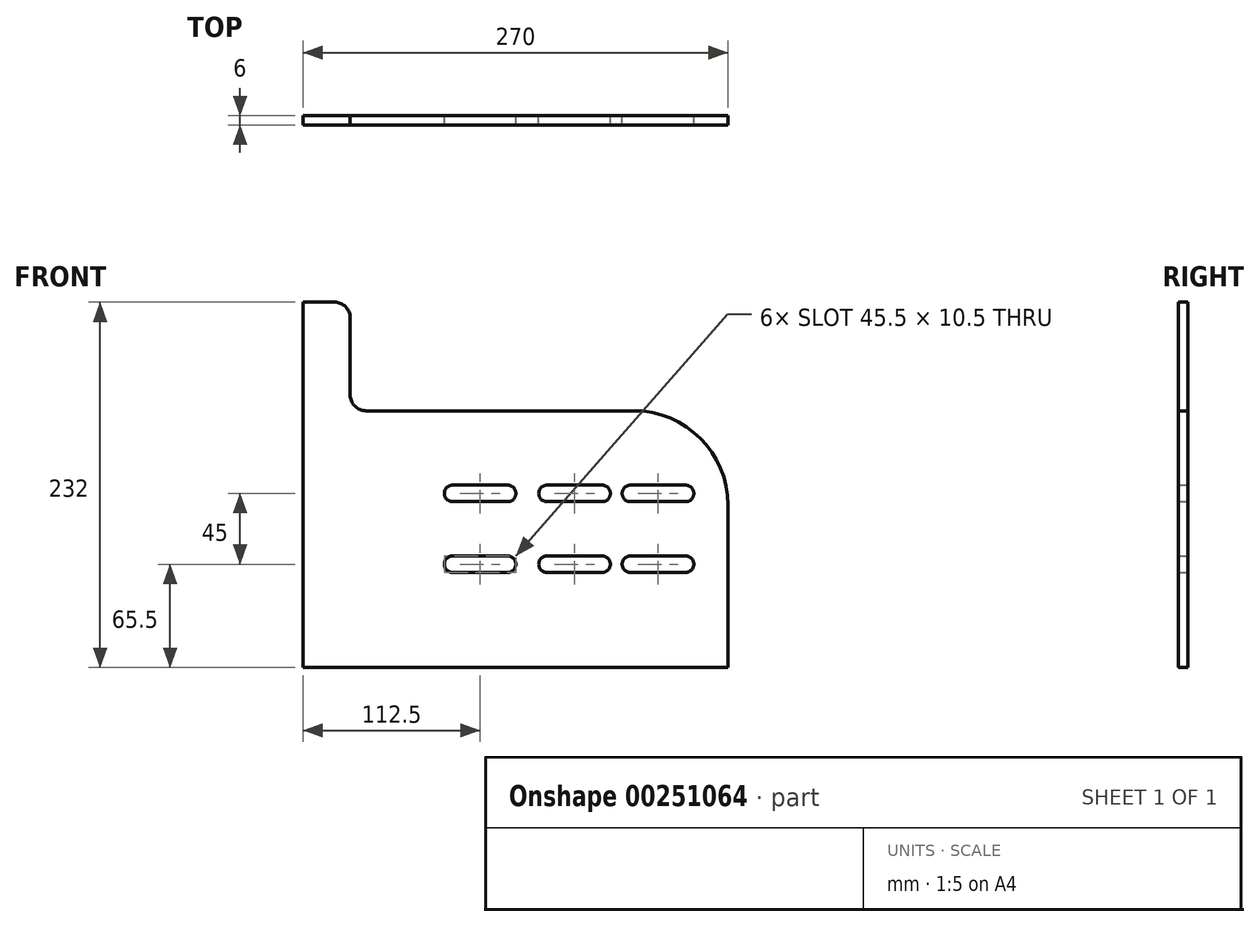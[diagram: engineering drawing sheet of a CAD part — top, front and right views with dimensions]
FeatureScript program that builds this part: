
annotation { "Feature Type Name" : "Feature", "Feature Type Description" : "" }
export const myFeature = defineFeature(function(context is Context, id is Id, definition is map)
    precondition{}
    {
        {
            var Q0;
            Q0=qCreatedBy(makeId("Front.planeOp"),FACE);
            var sketch = newSketch(context, id + "F0", { "sketchPlane" : qUnion([Q0])});
            skLineSegment(sketch, "E0.bottom", {"start": v(0, 0) * mm, "end": v(270, 0) * mm});
            skLineSegment(sketch, "E0.top", {"start": v(40, 163) * mm, "end": v(210, 163) * mm});
            skLineSegment(sketch, "E0.left", {"start": v(0, 0) * mm, "end": v(0, 163) * mm});
            skLineSegment(sketch, "E0.right", {"start": v(270, 0) * mm, "end": v(270, 103) * mm});
            skLineSegment(sketch, "E1.bottom", {"start": v(95, 115.75) * mm, "end": v(130, 115.75) * mm});
            skLineSegment(sketch, "E1.top", {"start": v(95, 105.25) * mm, "end": v(130, 105.25) * mm});
            skArc(sketch, "E2", {"start": v(95, 115.75) * mm, "mid": v(89.75, 110.5) * mm, "end": v(95, 105.25) * mm});
            skArc(sketch, "E3", {"start": v(130, 105.25) * mm, "mid": v(135.25, 110.5) * mm, "end": v(130, 115.75) * mm});
            skPoint(sketch, "E4.startSnap0", {"position": v(89.75, 110.5) * mm});
            skPoint(sketch, "E4.endSnap0", {"position": v(89.75, 110.5) * mm});
            skLineSegment(sketch, "E5", {"start": v(301.19, 88) * mm, "end": v(-50.1, 88) * mm, "construction": true});
            skLineSegment(sketch, "E6", {"start": v(71.88, 110.5) * mm, "end": v(250.88, 110.5) * mm, "construction": true});
            skLineSegment(sketch, "E7.1.0.0", {"start": v(155, 115.75) * mm, "end": v(190, 115.75) * mm});
            skLineSegment(sketch, "E7.1.0.1", {"start": v(155, 105.25) * mm, "end": v(190, 105.25) * mm});
            skArc(sketch, "E7.1.0.2", {"start": v(190, 105.25) * mm, "mid": v(195.25, 110.5) * mm, "end": v(190, 115.75) * mm});
            skArc(sketch, "E7.1.0.3", {"start": v(155, 115.75) * mm, "mid": v(149.75, 110.5) * mm, "end": v(155, 105.25) * mm});
            skPoint(sketch, "E7.1.0.4", {"position": v(149.75, 110.5) * mm});
            skPoint(sketch, "E7.1.0.5", {"position": v(149.75, 110.5) * mm});
            skLineSegment(sketch, "E7.direction1", {"start": v(95, 105.25) * mm, "end": v(155, 105.25) * mm, "construction": true});
            skArc(sketch, "E8.1.0.0", {"start": v(243, 105.25) * mm, "mid": v(248.25, 110.5) * mm, "end": v(243, 115.75) * mm});
            skPoint(sketch, "E8.1.0.1", {"position": v(202.75, 110.5) * mm});
            skArc(sketch, "E8.1.0.2", {"start": v(208, 115.75) * mm, "mid": v(202.75, 110.5) * mm, "end": v(208, 105.25) * mm});
            skLineSegment(sketch, "E8.1.0.3", {"start": v(208, 105.25) * mm, "end": v(243, 105.25) * mm});
            skLineSegment(sketch, "E8.1.0.4", {"start": v(208, 115.75) * mm, "end": v(243, 115.75) * mm});
            skPoint(sketch, "E8.1.0.5", {"position": v(202.75, 110.5) * mm});
            skLineSegment(sketch, "E8.direction1", {"start": v(155, 105.25) * mm, "end": v(208, 105.25) * mm, "construction": true});
            skPoint(sketch, "E9.MirrorP", {"position": v(202.75, 65.5) * mm});
            skLineSegment(sketch, "E10.MirrorCS", {"start": v(155, 70.75) * mm, "end": v(190, 70.75) * mm});
            skPoint(sketch, "E11.MirrorP", {"position": v(89.75, 65.5) * mm});
            skArc(sketch, "E12.MirrorCS", {"start": v(208, 60.25) * mm, "mid": v(202.75, 65.5) * mm, "end": v(208, 70.75) * mm});
            skLineSegment(sketch, "E13.MirrorCS", {"start": v(95, 70.75) * mm, "end": v(130, 70.75) * mm});
            skPoint(sketch, "E14.MirrorP", {"position": v(149.75, 65.5) * mm});
            skArc(sketch, "E15.MirrorCS", {"start": v(190, 70.75) * mm, "mid": v(195.25, 65.5) * mm, "end": v(190, 60.25) * mm});
            skLineSegment(sketch, "E16.MirrorCS", {"start": v(155, 70.75) * mm, "end": v(208, 70.75) * mm, "construction": true});
            skArc(sketch, "E17.MirrorCS", {"start": v(95, 60.25) * mm, "mid": v(89.75, 65.5) * mm, "end": v(95, 70.75) * mm});
            skArc(sketch, "E18.MirrorCS", {"start": v(243, 70.75) * mm, "mid": v(248.25, 65.5) * mm, "end": v(243, 60.25) * mm});
            skLineSegment(sketch, "E19.MirrorCS", {"start": v(71.88, 65.5) * mm, "end": v(250.88, 65.5) * mm, "construction": true});
            skLineSegment(sketch, "E20.MirrorCS", {"start": v(95, 70.75) * mm, "end": v(155, 70.75) * mm, "construction": true});
            skLineSegment(sketch, "E21.MirrorCS", {"start": v(208, 60.25) * mm, "end": v(243, 60.25) * mm});
            skLineSegment(sketch, "E22.MirrorCS", {"start": v(95, 60.25) * mm, "end": v(130, 60.25) * mm});
            skArc(sketch, "E23.MirrorCS", {"start": v(155, 60.25) * mm, "mid": v(149.75, 65.5) * mm, "end": v(155, 70.75) * mm});
            skLineSegment(sketch, "E24.MirrorCS", {"start": v(208, 70.75) * mm, "end": v(243, 70.75) * mm});
            skArc(sketch, "E25.MirrorCS", {"start": v(130, 70.75) * mm, "mid": v(135.25, 65.5) * mm, "end": v(130, 60.25) * mm});
            skLineSegment(sketch, "E26.MirrorCS", {"start": v(155, 60.25) * mm, "end": v(190, 60.25) * mm});
            skArc(sketch, "E27.filletArc", {"start": v(270, 103) * mm, "mid": v(252.43, 145.43) * mm, "end": v(210, 163) * mm});
            skLineSegment(sketch, "E28.top", {"start": v(20, 232) * mm, "end": v(0, 232) * mm});
            skLineSegment(sketch, "E29", {"start": v(30, 173) * mm, "end": v(30, 222) * mm});
            skLineSegment(sketch, "E30", {"start": v(0, 232) * mm, "end": v(0, 163) * mm});
            skArc(sketch, "E31.filletArc", {"start": v(30, 222) * mm, "mid": v(27.07, 229.07) * mm, "end": v(20, 232) * mm});
            skPoint(sketch, "E32.visualSharp", {"position": v(30, 163) * mm});
            skArc(sketch, "E32.filletArc", {"start": v(30, 173) * mm, "mid": v(32.93, 165.93) * mm, "end": v(40, 163) * mm});
            skSolve(sketch);
        }
        {
            var Q0;
            Q0=makeQuery(id+"F0.imprint","IMPRINT",FACE,{"disambiguationData":[TD([[makeQuery(id+"F0.imprint","IMPRINT",EDGE,{"derivedFrom":sQuery(id+"F0.wireOp",EDGE,"E0.bottom")}),1.0]])]});
            extrude(context, id + "F1", {"entities" : qUnion([Q0]), "depth" : 6 * mm});
        }
    });
